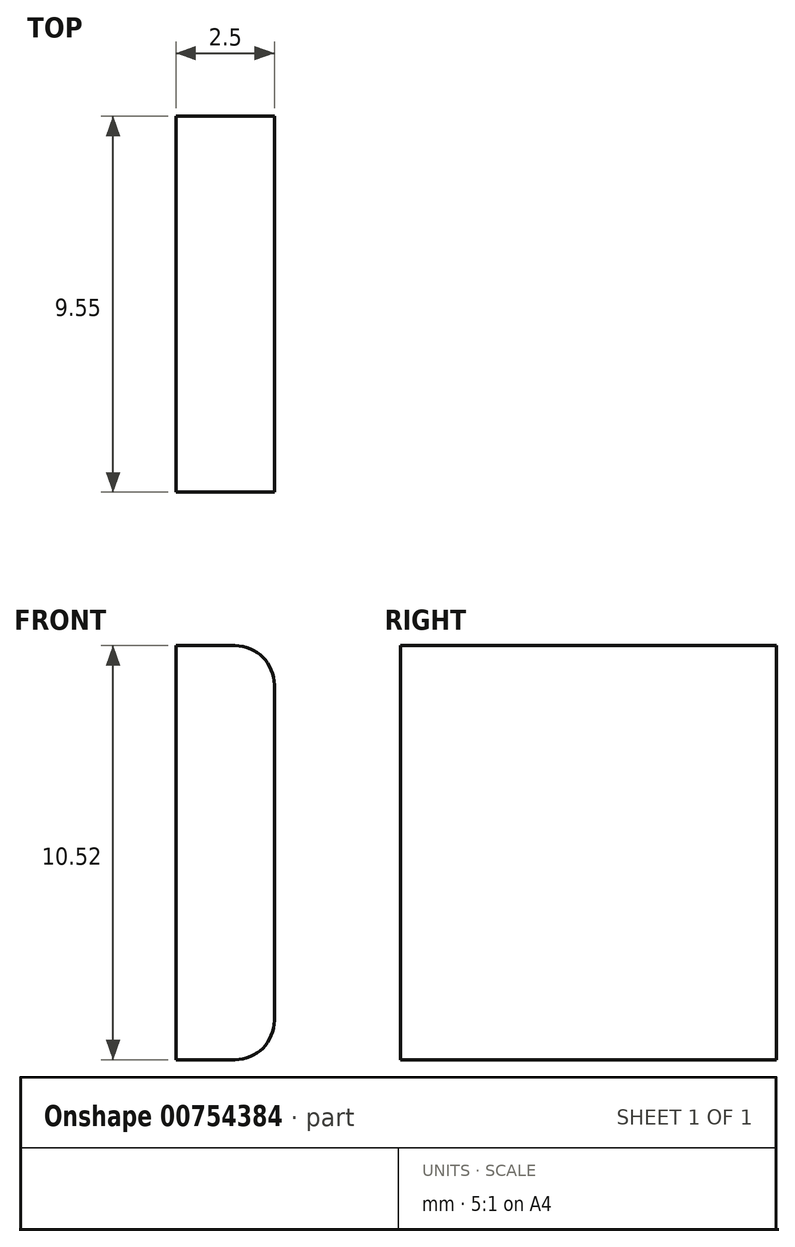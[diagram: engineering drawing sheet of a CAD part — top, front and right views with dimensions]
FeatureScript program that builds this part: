
annotation { "Feature Type Name" : "Feature", "Feature Type Description" : "" }
export const myFeature = defineFeature(function(context is Context, id is Id, definition is map)
    precondition{}
    {
        {
            var Q0;
            Q0=qCreatedBy(makeId("Front.planeOp"),FACE);
            var sketch = newSketch(context, id + "F0", { "sketchPlane" : qUnion([Q0])});
            skLineSegment(sketch, "E0", {"start": v(0, 0) * mm, "end": v(0, -5) * mm});
            skLineSegment(sketch, "E1", {"start": v(0, 0) * mm, "end": v(0, 5.52) * mm});
            skLineSegment(sketch, "E2", {"start": v(0, -5) * mm, "end": v(-1.5, -5) * mm});
            skLineSegment(sketch, "E3", {"start": v(0, 5.52) * mm, "end": v(-1.5, 5.52) * mm});
            skLineSegment(sketch, "E4", {"start": v(-2.5, 4.52) * mm, "end": v(-2.5, -4) * mm});
            skPoint(sketch, "E5.visualSharp", {"position": v(-2.5, 5.52) * mm});
            skArc(sketch, "E5.filletArc", {"start": v(-1.5, 5.52) * mm, "mid": v(-2.2, 5.22) * mm, "end": v(-2.5, 4.52) * mm});
            skPoint(sketch, "E6.visualSharp", {"position": v(-2.5, -5) * mm});
            skArc(sketch, "E6.filletArc", {"start": v(-2.5, -4) * mm, "mid": v(-2.2, -4.7) * mm, "end": v(-1.5, -5) * mm});
            skSolve(sketch);
        }
        {
            var Q0;
            Q0=qSketchRegion(id+"F0",true);
            extrude(context, id + "F1", {"entities" : qUnion([Q0]), "depth" : 9.55 * mm, "offsetDistance" : 25 * mm});
        }
        {
            var Q0;
            Q0=makeQuery(id+"F1.opExtrude","SWEPT_BODY",BODY,{"disambiguationData":[OSD([sQuery(id+"F0.wireOp",EDGE,"E0"),sQuery(id+"F0.wireOp",EDGE,"E1"),sQuery(id+"F0.wireOp",EDGE,"E2"),sQuery(id+"F0.wireOp",EDGE,"E3"),sQuery(id+"F0.wireOp",EDGE,"E4"),sQuery(id+"F0.wireOp",EDGE,"E5.filletArc"),sQuery(id+"F0.wireOp",EDGE,"E6.filletArc")])]});
            var Q1;
            Q1=qCreatedBy(makeId("Right.planeOp"),FACE);
            mirror(context, id + "F2", {"entities" : qUnion([Q0]), "mirrorPlane" : qUnion([Q1])});
        }
        {
            var Q0;
            Q0=makeQuery(id+"F1.opExtrude","SWEPT_BODY",BODY,{"disambiguationData":[OSD([sQuery(id+"F0.wireOp",EDGE,"E0"),sQuery(id+"F0.wireOp",EDGE,"E1"),sQuery(id+"F0.wireOp",EDGE,"E2"),sQuery(id+"F0.wireOp",EDGE,"E3"),sQuery(id+"F0.wireOp",EDGE,"E4"),sQuery(id+"F0.wireOp",EDGE,"E5.filletArc"),sQuery(id+"F0.wireOp",EDGE,"E6.filletArc")])]});
            deleteBodies(context, id + "F3", {"entities" : qUnion([Q0])});
        }
    });
